# Revit family: Recessed_Shelf-Whitehall-BestCare_DignitySuite-WHD-SHV15
name_source: partatom
category: Furniture
revit_build: Autodesk Revit 2018 (Build: 20170223_1515(x64)
units: mm (PartAtom-declared; Revit-internal decimal feet)

## family parameters
Cut with Voids When Loaded = No
Host = Face
OmniClass Number = 23.40.20.27.11
OmniClass Title = Shelves
Room Calculation Point = No
Shared = Yes

## types (1)
- WHD-SHV15
    -EG10 Snow White Enviro-glaze color (Shelf Backing) = No
    -MF Mirror Finish (Shelf Backing) = No
    -OCC Optional Corterra Color (Frame) Specify OCC = No
    Assembly Code = E2010
    Default Elevation = 0"
    Description = Ligature Resistant recessed shelf 15” width
    Frame Material = Polymer Resin Corterra-Whitehall-Blanco (OCC11)
    Height = 38"
    Installation Type = Wall Mounted
    Length = 15 1/4"
    Manufacturer = Whitehall Mfg.
    Model = WHD-SHV15
    Mounting Frame Material = Metal-Whitehall-Stainless Steel
    Price = Prices may vary. Please consult Manufacturer Representative for most up-to-date price list.
    Product Documentation Link = https://www.whitehallmfg.com
    Shelf Back Panel Material = Stainless Steel-Whitehall-Dignity Blue (EG-30)-Powder Coated
    URL = https://www.whitehallmfg.com
    Warranty Documentation Link = https://www.whitehallmfg.com
    Width = 6 1/2"

## geometry (parser evidence)
native form markers: Sweep x3
no freeform markers — native parametric forms only
